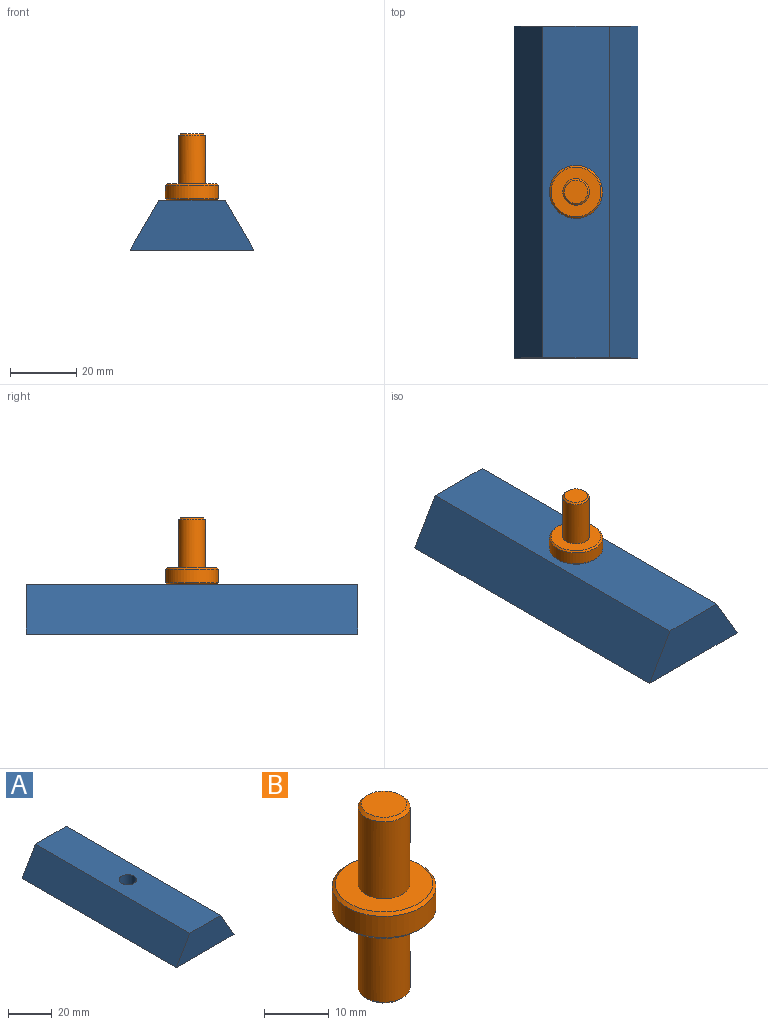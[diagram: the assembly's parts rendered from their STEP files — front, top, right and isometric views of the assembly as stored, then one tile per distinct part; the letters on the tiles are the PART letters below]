
ASSEMBLY  parts=2 mates=1
PART A: 7 faces, bbox 37.3x100x15 mm
  f0: plane 100x20mm, normal (0,0,1), area 1949.7mm2, adj f1,f3,f4,f5,f6
  f1: plane 100x15mm, normal (-0.87,0,0.5), area 1732.1mm2, adj f0,f2,f4,f5
  f2: plane 100x37.32mm, normal (0,0,-1), area 3681.8mm2, adj f1,f3,f4,f5,f6
  f3: plane 100x15mm, normal (0.87,0,0.5), area 1732.1mm2, adj f0,f2,f4,f5
  f4: plane 37.32x15mm, normal (0,-1,0), area 429.9mm2, adj f0,f1,f2,f3
  f5: plane 37.32x15mm, normal (0,1,0), area 429.9mm2, adj f0,f1,f2,f3
  f6: cylinder r=4mm len=15mm, axis (0,0,1), area 377mm2, adj f0,f2
PART B: 11 faces, bbox 16x16x35 mm
  f0: cylinder r=4mm len=14.5mm, axis (0,0,-1), area 364.4mm2, adj f3,f10
  f1: plane 7x7mm, normal (0,0,1), area 38.5mm2, adj f10
  f2: cylinder r=8mm len=16mm, axis (0,0,-1), area 201.1mm2, adj f7,f8
  f3: plane 15x15mm, normal (0,0,1), area 126.4mm2, adj f0,f8
  f4: plane 15x15mm, normal (0,0,-1), area 126.4mm2, adj f6,f7
  f5: plane 7x7mm, normal (0,0,-1), area 38.5mm2, adj f9
  f6: cylinder r=4mm len=14.5mm, axis (0,0,-1), area 364.4mm2, adj f4,f9
  f7: cone r=8mm half-angle=45deg, axis (0,0,1), area 34.4mm2, adj f2,f4
  f8: cone r=7.5mm half-angle=45deg, axis (0,0,-1), area 34.4mm2, adj f2,f3
  f9: cone r=4mm half-angle=45deg, axis (0,0,1), area 16.7mm2, adj f5,f6
  f10: cone r=3.5mm half-angle=45deg, axis (0,0,-1), area 16.7mm2, adj f0,f1
PLACE A at identity fixed
PLACE B at identity
MATE fastened B.f9 <-> A.f6  axis (0,0,-1) through (0,0,30)mm
